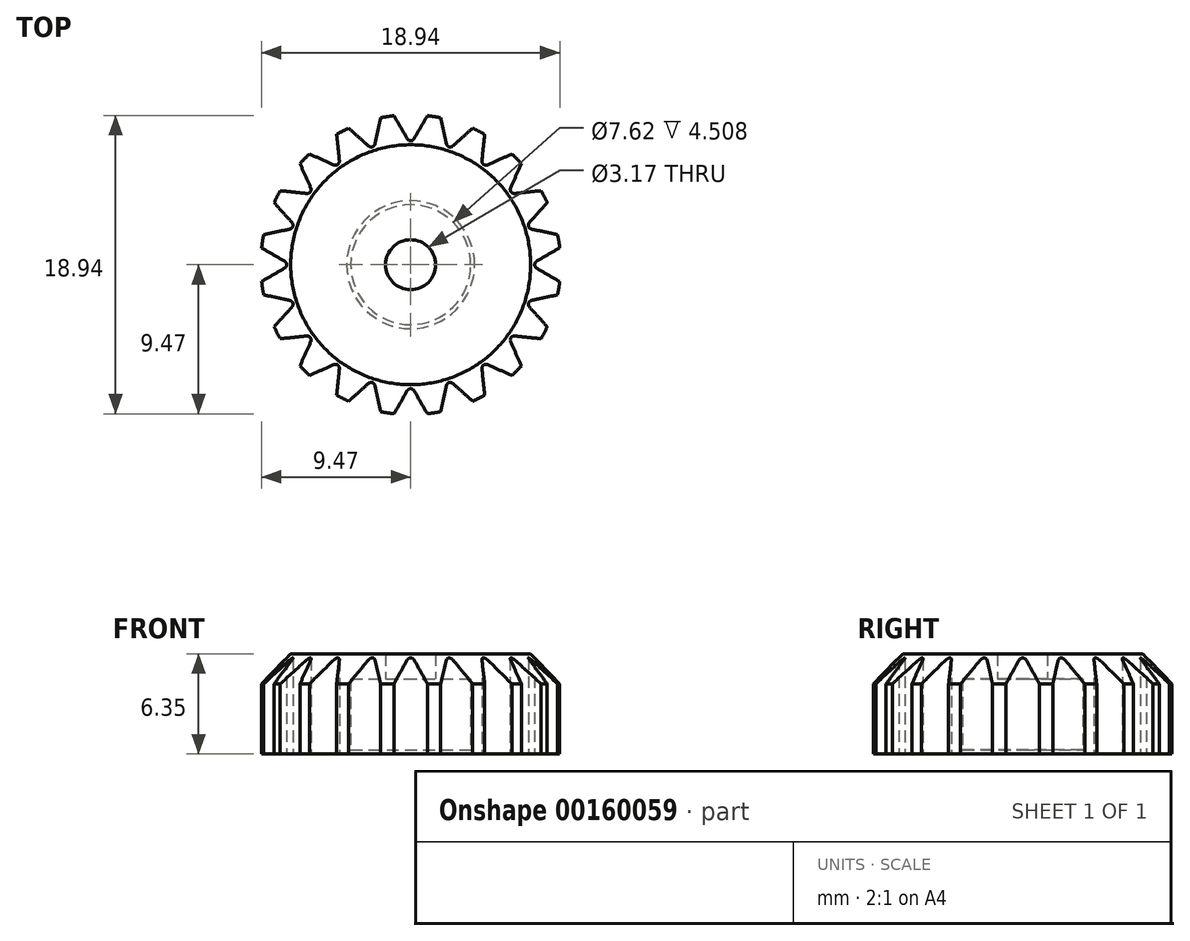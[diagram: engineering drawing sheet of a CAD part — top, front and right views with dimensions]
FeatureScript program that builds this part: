
annotation { "Feature Type Name" : "Feature", "Feature Type Description" : "" }
export const myFeature = defineFeature(function(context is Context, id is Id, definition is map)
    precondition{}
    {
        {
            var Q0;
            Q0=qCreatedBy(makeId("Front.planeOp"),FACE);
            var sketch = newSketch(context, id + "F0", { "sketchPlane" : qUnion([Q0])});
            skLineSegment(sketch, "E0", {"start": v(3.81, 0) * mm, "end": v(9.52, 0) * mm});
            skLineSegment(sketch, "E1", {"start": v(9.52, 0) * mm, "end": v(9.52, 6.35) * mm});
            skLineSegment(sketch, "E2", {"start": v(9.52, 6.35) * mm, "end": v(1.59, 6.35) * mm});
            skLineSegment(sketch, "E3", {"start": v(1.59, 6.35) * mm, "end": v(1.59, 4.76) * mm});
            skLineSegment(sketch, "E4", {"start": v(1.59, 4.76) * mm, "end": v(3.81, 4.76) * mm});
            skLineSegment(sketch, "E5", {"start": v(3.81, 4.76) * mm, "end": v(3.81, 0) * mm});
            skLineSegment(sketch, "E6", {"start": v(0, 0) * mm, "end": v(0, 52.4) * mm, "construction": true});
            skSolve(sketch);
        }
        {
            var Q0;
            Q0 = qSketchRegion(id + "F0", true);
            var Q1;
            Q1=sQuery(id+"F0.wireOp",EDGE,"E6");
            revolve(context, id + "F1", {"entities" : qUnion([Q0]), "axis" : qUnion([Q1]), "revolveType" : RevolveType.FULL});
        }
        {
            var Q0;
            Q0=makeQuery(id+"F1.opRevolve","SWEPT_EDGE",EDGE,{"disambiguationData":[OSD([sQuery(id+"F0.wireOp",EDGE,"E1"),sQuery(id+"F0.wireOp",EDGE,"E2")])]});
            chamfer(context, id + "F2", {"entities" : qUnion([Q0]), "width" : 1.9 * mm, "tangentPropagation" : true});
        }
        {
            var Q0;
            Q0=makeQuery(id+"F1.opRevolve","SWEPT_FACE",FACE,{"disambiguationData":[OSD([sQuery(id+"F0.wireOp",EDGE,"E2")])]});
            var sketch = newSketch(context, id + "F3", { "sketchPlane" : qUnion([Q0])});
            skLineSegment(sketch, "E7", {"start": v(0, 0) * mm, "end": v(0, 9.52) * mm, "construction": true});
            skLineSegment(sketch, "E8", {"start": v(-1.1, 9.52) * mm, "end": v(1.1, 9.52) * mm});
            skLineSegment(sketch, "E9", {"start": v(-1.1, 9.52) * mm, "end": v(0, 7.62) * mm});
            skLineSegment(sketch, "E10", {"start": v(0, 7.62) * mm, "end": v(1.1, 9.52) * mm});
            skCircle(sketch, "E11.0", {"center": v(0, 0) * mm, "radius": 9.52 * mm});
            skSolve(sketch);
        }
        {
            var Q0;
            {var subQ0=sQuery(id+"F3.wireOp",EDGE,"E10");var subQ1=sQuery(id+"F3.wireOp",EDGE,"E9");var subQ2=makeQuery(id+"F3.imprint","INTERSECT",VERTEX,{"derivedFrom":[subQ1,subQ0]});Q0=makeQuery(id+"F3.imprint","IMPRINT",FACE,{"disambiguationData":[TD([[makeQuery(id+"F3.imprint","IMPRINT",EDGE,{"disambiguationData":[TD([[subQ2,1.0]])],"derivedFrom":subQ1}),1.0]])]});}
            var Q1;
            {var subQ0=sQuery(id+"F3.wireOp",EDGE,"E11.0");var subQ1=makeQuery(id+"F3.imprint","INTERSECT",VERTEX,{"derivedFrom":[sQuery(id+"F3.wireOp",EDGE,"E8"),subQ0]});Q1=makeQuery(id+"F3.imprint","IMPRINT",FACE,{"disambiguationData":[TD([[makeQuery(id+"F3.imprint","IMPRINT",EDGE,{"disambiguationData":[TD([[subQ1,1.0]])],"derivedFrom":subQ0}),1.0]])]});}
            var Q2;
            Q2=makeQuery(id+"F1.opRevolve","SWEPT_FACE",FACE,{"disambiguationData":[OSD([sQuery(id+"F0.wireOp",EDGE,"E0")])]});
            extrude(context, id + "F4", {"entities" : qUnion([Q0, Q1]), "endBound" : BoundingType.UP_TO_SURFACE, "oppositeDirection" : true, "endBoundEntityFace" : qUnion([Q2]), "depth" : 25.4 * mm});
        }
        {
            var Q0;
            Q0=makeQuery(id+"F4.opExtrude","SWEPT_BODY",BODY,{"disambiguationData":[OSD([sQuery(id+"F3.wireOp",EDGE,"cd4487d4-f061-4d57-82fb-461e1aad9f84.0.0"),sQuery(id+"F3.wireOp",EDGE,"E9"),sQuery(id+"F3.wireOp",EDGE,"E10")])]});
            var Q1;
            Q1=makeQuery(id+"F1.opRevolve","SWEPT_FACE",FACE,{"disambiguationData":[OSD([sQuery(id+"F0.wireOp",EDGE,"E1")])]});
            circularPattern(context, id + "F5", {"entities" : qUnion([Q0]), "axis" : qUnion([Q1]), "angle" : 360 * degree, "instanceCount" : 20, "equalSpace" : true});
        }
        {
            var Q0;
            Q0=makeQuery(id+"F4.opExtrude","SWEPT_BODY",BODY,{"disambiguationData":[OSD([sQuery(id+"F3.wireOp",EDGE,"cd4487d4-f061-4d57-82fb-461e1aad9f84.0.0"),sQuery(id+"F3.wireOp",EDGE,"E9"),sQuery(id+"F3.wireOp",EDGE,"E10")])]});
            var Q1;
            Q1=makeQuery(id+"F5.opPattern","COPY",BODY,{"derivedFrom":makeQuery(id+"F4.opExtrude","SWEPT_BODY",BODY,{"disambiguationData":[OSD([sQuery(id+"F3.wireOp",EDGE,"cd4487d4-f061-4d57-82fb-461e1aad9f84.0.0"),sQuery(id+"F3.wireOp",EDGE,"E9"),sQuery(id+"F3.wireOp",EDGE,"E10")])]}),"instanceName":"1"});
            var Q2;
            Q2=makeQuery(id+"F5.opPattern","COPY",BODY,{"derivedFrom":makeQuery(id+"F4.opExtrude","SWEPT_BODY",BODY,{"disambiguationData":[OSD([sQuery(id+"F3.wireOp",EDGE,"cd4487d4-f061-4d57-82fb-461e1aad9f84.0.0"),sQuery(id+"F3.wireOp",EDGE,"E9"),sQuery(id+"F3.wireOp",EDGE,"E10")])]}),"instanceName":"2"});
            var Q3;
            Q3=makeQuery(id+"F5.opPattern","COPY",BODY,{"derivedFrom":makeQuery(id+"F4.opExtrude","SWEPT_BODY",BODY,{"disambiguationData":[OSD([sQuery(id+"F3.wireOp",EDGE,"cd4487d4-f061-4d57-82fb-461e1aad9f84.0.0"),sQuery(id+"F3.wireOp",EDGE,"E9"),sQuery(id+"F3.wireOp",EDGE,"E10")])]}),"instanceName":"3"});
            var Q4;
            Q4=makeQuery(id+"F5.opPattern","COPY",BODY,{"derivedFrom":makeQuery(id+"F4.opExtrude","SWEPT_BODY",BODY,{"disambiguationData":[OSD([sQuery(id+"F3.wireOp",EDGE,"cd4487d4-f061-4d57-82fb-461e1aad9f84.0.0"),sQuery(id+"F3.wireOp",EDGE,"E9"),sQuery(id+"F3.wireOp",EDGE,"E10")])]}),"instanceName":"4"});
            var Q5;
            Q5=makeQuery(id+"F5.opPattern","COPY",BODY,{"derivedFrom":makeQuery(id+"F4.opExtrude","SWEPT_BODY",BODY,{"disambiguationData":[OSD([sQuery(id+"F3.wireOp",EDGE,"cd4487d4-f061-4d57-82fb-461e1aad9f84.0.0"),sQuery(id+"F3.wireOp",EDGE,"E9"),sQuery(id+"F3.wireOp",EDGE,"E10")])]}),"instanceName":"5"});
            var Q6;
            Q6=makeQuery(id+"F5.opPattern","COPY",BODY,{"derivedFrom":makeQuery(id+"F4.opExtrude","SWEPT_BODY",BODY,{"disambiguationData":[OSD([sQuery(id+"F3.wireOp",EDGE,"cd4487d4-f061-4d57-82fb-461e1aad9f84.0.0"),sQuery(id+"F3.wireOp",EDGE,"E9"),sQuery(id+"F3.wireOp",EDGE,"E10")])]}),"instanceName":"6"});
            var Q7;
            Q7=makeQuery(id+"F5.opPattern","COPY",BODY,{"derivedFrom":makeQuery(id+"F4.opExtrude","SWEPT_BODY",BODY,{"disambiguationData":[OSD([sQuery(id+"F3.wireOp",EDGE,"cd4487d4-f061-4d57-82fb-461e1aad9f84.0.0"),sQuery(id+"F3.wireOp",EDGE,"E9"),sQuery(id+"F3.wireOp",EDGE,"E10")])]}),"instanceName":"7"});
            var Q8;
            Q8=makeQuery(id+"F5.opPattern","COPY",BODY,{"derivedFrom":makeQuery(id+"F4.opExtrude","SWEPT_BODY",BODY,{"disambiguationData":[OSD([sQuery(id+"F3.wireOp",EDGE,"cd4487d4-f061-4d57-82fb-461e1aad9f84.0.0"),sQuery(id+"F3.wireOp",EDGE,"E9"),sQuery(id+"F3.wireOp",EDGE,"E10")])]}),"instanceName":"8"});
            var Q9;
            Q9=makeQuery(id+"F5.opPattern","COPY",BODY,{"derivedFrom":makeQuery(id+"F4.opExtrude","SWEPT_BODY",BODY,{"disambiguationData":[OSD([sQuery(id+"F3.wireOp",EDGE,"cd4487d4-f061-4d57-82fb-461e1aad9f84.0.0"),sQuery(id+"F3.wireOp",EDGE,"E9"),sQuery(id+"F3.wireOp",EDGE,"E10")])]}),"instanceName":"9"});
            var Q10;
            Q10=makeQuery(id+"F5.opPattern","COPY",BODY,{"derivedFrom":makeQuery(id+"F4.opExtrude","SWEPT_BODY",BODY,{"disambiguationData":[OSD([sQuery(id+"F3.wireOp",EDGE,"cd4487d4-f061-4d57-82fb-461e1aad9f84.0.0"),sQuery(id+"F3.wireOp",EDGE,"E9"),sQuery(id+"F3.wireOp",EDGE,"E10")])]}),"instanceName":"10"});
            var Q11;
            Q11=makeQuery(id+"F5.opPattern","COPY",BODY,{"derivedFrom":makeQuery(id+"F4.opExtrude","SWEPT_BODY",BODY,{"disambiguationData":[OSD([sQuery(id+"F3.wireOp",EDGE,"cd4487d4-f061-4d57-82fb-461e1aad9f84.0.0"),sQuery(id+"F3.wireOp",EDGE,"E9"),sQuery(id+"F3.wireOp",EDGE,"E10")])]}),"instanceName":"11"});
            var Q12;
            Q12=makeQuery(id+"F5.opPattern","COPY",BODY,{"derivedFrom":makeQuery(id+"F4.opExtrude","SWEPT_BODY",BODY,{"disambiguationData":[OSD([sQuery(id+"F3.wireOp",EDGE,"cd4487d4-f061-4d57-82fb-461e1aad9f84.0.0"),sQuery(id+"F3.wireOp",EDGE,"E9"),sQuery(id+"F3.wireOp",EDGE,"E10")])]}),"instanceName":"12"});
            var Q13;
            Q13=makeQuery(id+"F5.opPattern","COPY",BODY,{"derivedFrom":makeQuery(id+"F4.opExtrude","SWEPT_BODY",BODY,{"disambiguationData":[OSD([sQuery(id+"F3.wireOp",EDGE,"cd4487d4-f061-4d57-82fb-461e1aad9f84.0.0"),sQuery(id+"F3.wireOp",EDGE,"E9"),sQuery(id+"F3.wireOp",EDGE,"E10")])]}),"instanceName":"13"});
            var Q14;
            Q14=makeQuery(id+"F5.opPattern","COPY",BODY,{"derivedFrom":makeQuery(id+"F4.opExtrude","SWEPT_BODY",BODY,{"disambiguationData":[OSD([sQuery(id+"F3.wireOp",EDGE,"cd4487d4-f061-4d57-82fb-461e1aad9f84.0.0"),sQuery(id+"F3.wireOp",EDGE,"E9"),sQuery(id+"F3.wireOp",EDGE,"E10")])]}),"instanceName":"14"});
            var Q15;
            Q15=makeQuery(id+"F5.opPattern","COPY",BODY,{"derivedFrom":makeQuery(id+"F4.opExtrude","SWEPT_BODY",BODY,{"disambiguationData":[OSD([sQuery(id+"F3.wireOp",EDGE,"cd4487d4-f061-4d57-82fb-461e1aad9f84.0.0"),sQuery(id+"F3.wireOp",EDGE,"E9"),sQuery(id+"F3.wireOp",EDGE,"E10")])]}),"instanceName":"15"});
            var Q16;
            Q16=makeQuery(id+"F5.opPattern","COPY",BODY,{"derivedFrom":makeQuery(id+"F4.opExtrude","SWEPT_BODY",BODY,{"disambiguationData":[OSD([sQuery(id+"F3.wireOp",EDGE,"cd4487d4-f061-4d57-82fb-461e1aad9f84.0.0"),sQuery(id+"F3.wireOp",EDGE,"E9"),sQuery(id+"F3.wireOp",EDGE,"E10")])]}),"instanceName":"16"});
            var Q17;
            Q17=makeQuery(id+"F5.opPattern","COPY",BODY,{"derivedFrom":makeQuery(id+"F4.opExtrude","SWEPT_BODY",BODY,{"disambiguationData":[OSD([sQuery(id+"F3.wireOp",EDGE,"cd4487d4-f061-4d57-82fb-461e1aad9f84.0.0"),sQuery(id+"F3.wireOp",EDGE,"E9"),sQuery(id+"F3.wireOp",EDGE,"E10")])]}),"instanceName":"17"});
            var Q18;
            Q18=makeQuery(id+"F5.opPattern","COPY",BODY,{"derivedFrom":makeQuery(id+"F4.opExtrude","SWEPT_BODY",BODY,{"disambiguationData":[OSD([sQuery(id+"F3.wireOp",EDGE,"cd4487d4-f061-4d57-82fb-461e1aad9f84.0.0"),sQuery(id+"F3.wireOp",EDGE,"E9"),sQuery(id+"F3.wireOp",EDGE,"E10")])]}),"instanceName":"18"});
            var Q19;
            Q19=makeQuery(id+"F5.opPattern","COPY",BODY,{"derivedFrom":makeQuery(id+"F4.opExtrude","SWEPT_BODY",BODY,{"disambiguationData":[OSD([sQuery(id+"F3.wireOp",EDGE,"cd4487d4-f061-4d57-82fb-461e1aad9f84.0.0"),sQuery(id+"F3.wireOp",EDGE,"E9"),sQuery(id+"F3.wireOp",EDGE,"E10")])]}),"instanceName":"19"});
            var Q20;
            Q20=makeQuery(id+"F1.opRevolve","SWEPT_BODY",BODY,{"disambiguationData":[OSD([sQuery(id+"F0.wireOp",EDGE,"E0"),sQuery(id+"F0.wireOp",EDGE,"E1"),sQuery(id+"F0.wireOp",EDGE,"E2"),sQuery(id+"F0.wireOp",EDGE,"E3"),sQuery(id+"F0.wireOp",EDGE,"E4"),sQuery(id+"F0.wireOp",EDGE,"E5")])]});
            booleanBodies(context, id + "F6", {"operationType" : BooleanOperationType.SUBTRACTION, "tools" : qUnion([Q0, Q1, Q2, Q3, Q4, Q5, Q6, Q7, Q8, Q9, Q10, Q11, Q12, Q13, Q14, Q15, Q16, Q17, Q18, Q19]), "targets" : qUnion([Q20])});
        }
        {
            var Q0;
            Q0=makeQuery(id+"F1.opRevolve","SWEPT_EDGE",EDGE,{"disambiguationData":[OSD([sQuery(id+"F0.wireOp",EDGE,"E0"),sQuery(id+"F0.wireOp",EDGE,"E5")])]});
            chamfer(context, id + "F7", {"entities" : qUnion([Q0]), "width" : 0.25 * mm, "tangentPropagation" : true});
        }
        {
            var Q0;
            Q0=makeQuery(id+"F6.opBoolean","COPY",EDGE,{"derivedFrom":makeQuery(id+"F5.opPattern","COPY",EDGE,{"derivedFrom":makeQuery(id+"F4.opExtrude","SWEPT_EDGE",EDGE,{"disambiguationData":[OSD([sQuery(id+"F0.wireOp",EDGE,"E1"),sQuery(id+"F0.wireOp",EDGE,"E2"),sQuery(id+"F3.wireOp",EDGE,"E9"),sQuery(id+"F3.wireOp",EDGE,"E10")])]}),"instanceName":"11"})});
            var Q1;
            Q1=makeQuery(id+"F6.opBoolean","COPY",EDGE,{"derivedFrom":makeQuery(id+"F5.opPattern","COPY",EDGE,{"derivedFrom":makeQuery(id+"F4.opExtrude","SWEPT_EDGE",EDGE,{"disambiguationData":[OSD([sQuery(id+"F0.wireOp",EDGE,"E1"),sQuery(id+"F0.wireOp",EDGE,"E2"),sQuery(id+"F3.wireOp",EDGE,"E9"),sQuery(id+"F3.wireOp",EDGE,"E10")])]}),"instanceName":"10"})});
            var Q2;
            Q2=makeQuery(id+"F6.opBoolean","COPY",EDGE,{"derivedFrom":makeQuery(id+"F5.opPattern","COPY",EDGE,{"derivedFrom":makeQuery(id+"F4.opExtrude","SWEPT_EDGE",EDGE,{"disambiguationData":[OSD([sQuery(id+"F0.wireOp",EDGE,"E1"),sQuery(id+"F0.wireOp",EDGE,"E2"),sQuery(id+"F3.wireOp",EDGE,"E9"),sQuery(id+"F3.wireOp",EDGE,"E10")])]}),"instanceName":"9"})});
            var Q3;
            Q3=makeQuery(id+"F6.opBoolean","COPY",EDGE,{"derivedFrom":makeQuery(id+"F5.opPattern","COPY",EDGE,{"derivedFrom":makeQuery(id+"F4.opExtrude","SWEPT_EDGE",EDGE,{"disambiguationData":[OSD([sQuery(id+"F0.wireOp",EDGE,"E1"),sQuery(id+"F0.wireOp",EDGE,"E2"),sQuery(id+"F3.wireOp",EDGE,"E9"),sQuery(id+"F3.wireOp",EDGE,"E10")])]}),"instanceName":"8"})});
            var Q4;
            Q4=makeQuery(id+"F6.opBoolean","COPY",EDGE,{"derivedFrom":makeQuery(id+"F5.opPattern","COPY",EDGE,{"derivedFrom":makeQuery(id+"F4.opExtrude","SWEPT_EDGE",EDGE,{"disambiguationData":[OSD([sQuery(id+"F0.wireOp",EDGE,"E1"),sQuery(id+"F0.wireOp",EDGE,"E2"),sQuery(id+"F3.wireOp",EDGE,"E9"),sQuery(id+"F3.wireOp",EDGE,"E10")])]}),"instanceName":"7"})});
            var Q5;
            Q5=makeQuery(id+"F6.opBoolean","COPY",EDGE,{"derivedFrom":makeQuery(id+"F5.opPattern","COPY",EDGE,{"derivedFrom":makeQuery(id+"F4.opExtrude","SWEPT_EDGE",EDGE,{"disambiguationData":[OSD([sQuery(id+"F0.wireOp",EDGE,"E1"),sQuery(id+"F0.wireOp",EDGE,"E2"),sQuery(id+"F3.wireOp",EDGE,"E9"),sQuery(id+"F3.wireOp",EDGE,"E10")])]}),"instanceName":"5"})});
            var Q6;
            Q6=makeQuery(id+"F6.opBoolean","COPY",EDGE,{"derivedFrom":makeQuery(id+"F5.opPattern","COPY",EDGE,{"derivedFrom":makeQuery(id+"F4.opExtrude","SWEPT_EDGE",EDGE,{"disambiguationData":[OSD([sQuery(id+"F0.wireOp",EDGE,"E1"),sQuery(id+"F0.wireOp",EDGE,"E2"),sQuery(id+"F3.wireOp",EDGE,"E9"),sQuery(id+"F3.wireOp",EDGE,"E10")])]}),"instanceName":"4"})});
            var Q7;
            Q7=makeQuery(id+"F6.opBoolean","COPY",EDGE,{"derivedFrom":makeQuery(id+"F5.opPattern","COPY",EDGE,{"derivedFrom":makeQuery(id+"F4.opExtrude","SWEPT_EDGE",EDGE,{"disambiguationData":[OSD([sQuery(id+"F0.wireOp",EDGE,"E1"),sQuery(id+"F0.wireOp",EDGE,"E2"),sQuery(id+"F3.wireOp",EDGE,"E9"),sQuery(id+"F3.wireOp",EDGE,"E10")])]}),"instanceName":"3"})});
            var Q8;
            Q8=makeQuery(id+"F6.opBoolean","COPY",EDGE,{"derivedFrom":makeQuery(id+"F5.opPattern","COPY",EDGE,{"derivedFrom":makeQuery(id+"F4.opExtrude","SWEPT_EDGE",EDGE,{"disambiguationData":[OSD([sQuery(id+"F0.wireOp",EDGE,"E1"),sQuery(id+"F0.wireOp",EDGE,"E2"),sQuery(id+"F3.wireOp",EDGE,"E9"),sQuery(id+"F3.wireOp",EDGE,"E10")])]}),"instanceName":"6"})});
            var Q9;
            Q9=makeQuery(id+"F6.opBoolean","COPY",EDGE,{"derivedFrom":makeQuery(id+"F5.opPattern","COPY",EDGE,{"derivedFrom":makeQuery(id+"F4.opExtrude","SWEPT_EDGE",EDGE,{"disambiguationData":[OSD([sQuery(id+"F0.wireOp",EDGE,"E1"),sQuery(id+"F0.wireOp",EDGE,"E2"),sQuery(id+"F3.wireOp",EDGE,"E9"),sQuery(id+"F3.wireOp",EDGE,"E10")])]}),"instanceName":"2"})});
            var Q10;
            Q10=makeQuery(id+"F6.opBoolean","COPY",EDGE,{"derivedFrom":makeQuery(id+"F5.opPattern","COPY",EDGE,{"derivedFrom":makeQuery(id+"F4.opExtrude","SWEPT_EDGE",EDGE,{"disambiguationData":[OSD([sQuery(id+"F0.wireOp",EDGE,"E1"),sQuery(id+"F0.wireOp",EDGE,"E2"),sQuery(id+"F3.wireOp",EDGE,"E9"),sQuery(id+"F3.wireOp",EDGE,"E10")])]}),"instanceName":"1"})});
            var Q11;
            Q11=makeQuery(id+"F6.opBoolean","COPY",EDGE,{"derivedFrom":makeQuery(id+"F4.opExtrude","SWEPT_EDGE",EDGE,{"disambiguationData":[OSD([sQuery(id+"F0.wireOp",EDGE,"E1"),sQuery(id+"F0.wireOp",EDGE,"E2"),sQuery(id+"F3.wireOp",EDGE,"E9"),sQuery(id+"F3.wireOp",EDGE,"E10")])]})});
            var Q12;
            Q12=makeQuery(id+"F6.opBoolean","COPY",EDGE,{"derivedFrom":makeQuery(id+"F5.opPattern","COPY",EDGE,{"derivedFrom":makeQuery(id+"F4.opExtrude","SWEPT_EDGE",EDGE,{"disambiguationData":[OSD([sQuery(id+"F0.wireOp",EDGE,"E1"),sQuery(id+"F0.wireOp",EDGE,"E2"),sQuery(id+"F3.wireOp",EDGE,"E9"),sQuery(id+"F3.wireOp",EDGE,"E10")])]}),"instanceName":"19"})});
            var Q13;
            Q13=makeQuery(id+"F6.opBoolean","COPY",EDGE,{"derivedFrom":makeQuery(id+"F5.opPattern","COPY",EDGE,{"derivedFrom":makeQuery(id+"F4.opExtrude","SWEPT_EDGE",EDGE,{"disambiguationData":[OSD([sQuery(id+"F0.wireOp",EDGE,"E1"),sQuery(id+"F0.wireOp",EDGE,"E2"),sQuery(id+"F3.wireOp",EDGE,"E9"),sQuery(id+"F3.wireOp",EDGE,"E10")])]}),"instanceName":"18"})});
            var Q14;
            Q14=makeQuery(id+"F6.opBoolean","COPY",EDGE,{"derivedFrom":makeQuery(id+"F5.opPattern","COPY",EDGE,{"derivedFrom":makeQuery(id+"F4.opExtrude","SWEPT_EDGE",EDGE,{"disambiguationData":[OSD([sQuery(id+"F0.wireOp",EDGE,"E1"),sQuery(id+"F0.wireOp",EDGE,"E2"),sQuery(id+"F3.wireOp",EDGE,"E9"),sQuery(id+"F3.wireOp",EDGE,"E10")])]}),"instanceName":"16"})});
            var Q15;
            Q15=makeQuery(id+"F6.opBoolean","COPY",EDGE,{"derivedFrom":makeQuery(id+"F5.opPattern","COPY",EDGE,{"derivedFrom":makeQuery(id+"F4.opExtrude","SWEPT_EDGE",EDGE,{"disambiguationData":[OSD([sQuery(id+"F0.wireOp",EDGE,"E1"),sQuery(id+"F0.wireOp",EDGE,"E2"),sQuery(id+"F3.wireOp",EDGE,"E9"),sQuery(id+"F3.wireOp",EDGE,"E10")])]}),"instanceName":"15"})});
            var Q16;
            Q16=makeQuery(id+"F6.opBoolean","COPY",EDGE,{"derivedFrom":makeQuery(id+"F5.opPattern","COPY",EDGE,{"derivedFrom":makeQuery(id+"F4.opExtrude","SWEPT_EDGE",EDGE,{"disambiguationData":[OSD([sQuery(id+"F0.wireOp",EDGE,"E1"),sQuery(id+"F0.wireOp",EDGE,"E2"),sQuery(id+"F3.wireOp",EDGE,"E9"),sQuery(id+"F3.wireOp",EDGE,"E10")])]}),"instanceName":"14"})});
            var Q17;
            Q17=makeQuery(id+"F6.opBoolean","COPY",EDGE,{"derivedFrom":makeQuery(id+"F5.opPattern","COPY",EDGE,{"derivedFrom":makeQuery(id+"F4.opExtrude","SWEPT_EDGE",EDGE,{"disambiguationData":[OSD([sQuery(id+"F0.wireOp",EDGE,"E1"),sQuery(id+"F0.wireOp",EDGE,"E2"),sQuery(id+"F3.wireOp",EDGE,"E9"),sQuery(id+"F3.wireOp",EDGE,"E10")])]}),"instanceName":"13"})});
            var Q18;
            Q18=makeQuery(id+"F6.opBoolean","COPY",EDGE,{"derivedFrom":makeQuery(id+"F5.opPattern","COPY",EDGE,{"derivedFrom":makeQuery(id+"F4.opExtrude","SWEPT_EDGE",EDGE,{"disambiguationData":[OSD([sQuery(id+"F0.wireOp",EDGE,"E1"),sQuery(id+"F0.wireOp",EDGE,"E2"),sQuery(id+"F3.wireOp",EDGE,"E9"),sQuery(id+"F3.wireOp",EDGE,"E10")])]}),"instanceName":"12"})});
            var Q19;
            Q19=makeQuery(id+"F6.opBoolean","COPY",EDGE,{"derivedFrom":makeQuery(id+"F5.opPattern","COPY",EDGE,{"derivedFrom":makeQuery(id+"F4.opExtrude","SWEPT_EDGE",EDGE,{"disambiguationData":[OSD([sQuery(id+"F0.wireOp",EDGE,"E1"),sQuery(id+"F0.wireOp",EDGE,"E2"),sQuery(id+"F3.wireOp",EDGE,"E9"),sQuery(id+"F3.wireOp",EDGE,"E10")])]}),"instanceName":"17"})});
            fillet(context, id + "F8", {"entities" : qUnion([Q0, Q1, Q2, Q3, Q4, Q5, Q6, Q7, Q8, Q9, Q10, Q11, Q12, Q13, Q14, Q15, Q16, Q17, Q18, Q19]), "radius" : 0.25 * mm, "tangentPropagation" : true, "allowEdgeOverflow" : false});
        }
    });
